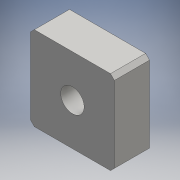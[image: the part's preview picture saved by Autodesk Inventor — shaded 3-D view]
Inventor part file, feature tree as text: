
AUTODESK INVENTOR PART (.ipt)
format: ipt  version: 2016 (Build 200138000, 138)  size: 103,936 bytes
history: native  units: mm
features: chamfer x4, extrude x2, sketch x2, other x1
ambient origin geometry x8: Origin, YZ Plane, XZ Plane, XY Plane, X Axis, Y Axis, Z Axis, Center Point
bodies: Body1 (feature_tree)
feature tree (9):
  other  "ソリッド1"
  extrude  "押し出し1"  Depth=43.0mm
  chamfer  "面取り1"  Distance=43.0mm
  chamfer  "面取り2"  Distance=18.0mm
  chamfer  "面取り3"  Distance=2.0mm Angle=45.0deg
  chamfer  "面取り4"  Distance=2.0mm Angle=45.0deg
  extrude  "押し出し2"  Depth=2.0mm TaperAngle=45.0deg
  sketch  "スケッチ1"
  sketch  "スケッチ2"
